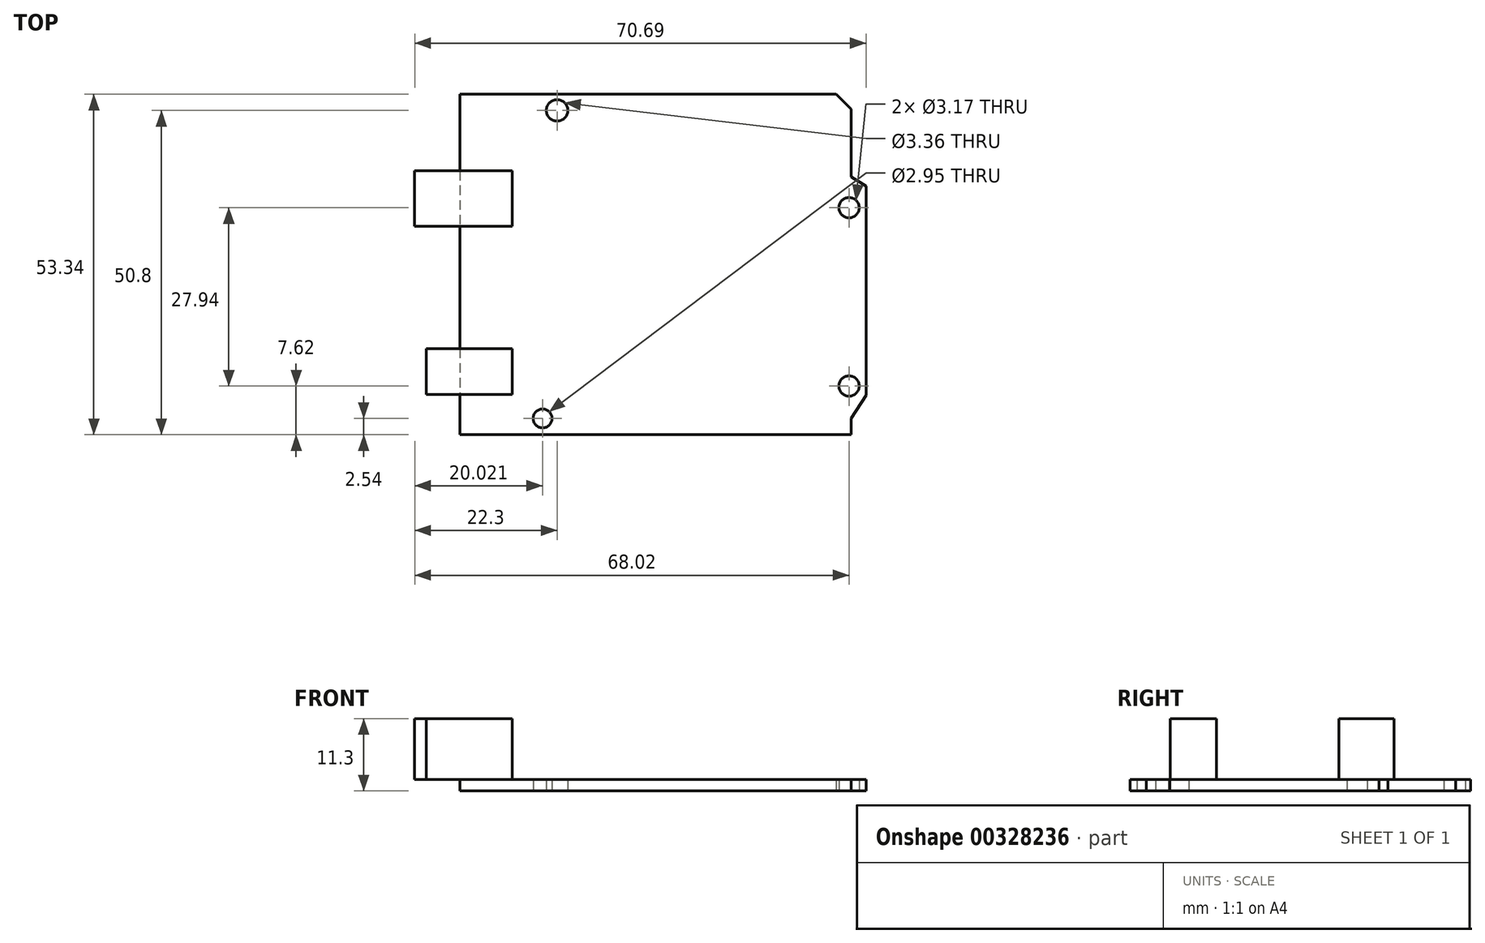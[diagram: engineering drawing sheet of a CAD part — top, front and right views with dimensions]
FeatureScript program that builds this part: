
annotation { "Feature Type Name" : "Feature", "Feature Type Description" : "" }
export const myFeature = defineFeature(function(context is Context, id is Id, definition is map)
    precondition{}
    {
        {
            var Q0;
            Q0=qCreatedBy(makeId("Top.planeOp"),FACE);
            var sketch = newSketch(context, id + "F0", { "sketchPlane" : qUnion([Q0])});
            skLineSegment(sketch, "E0", {"start": v(0, 0) * mm, "end": v(61.27, 0) * mm});
            skLineSegment(sketch, "E1", {"start": v(61.27, 0) * mm, "end": v(61.27, 2.54) * mm});
            skLineSegment(sketch, "E2", {"start": v(0, 53.34) * mm, "end": v(58.91, 53.34) * mm});
            skLineSegment(sketch, "E3", {"start": v(61.27, 50.98) * mm, "end": v(61.27, 40.38) * mm});
            skLineSegment(sketch, "E4", {"start": v(58.91, 53.34) * mm, "end": v(61.27, 50.98) * mm});
            skPoint(sketch, "E5", {"position": v(63.63, 38.97) * mm});
            skLineSegment(sketch, "E6", {"start": v(61.27, 40.38) * mm, "end": v(63.63, 38.97) * mm});
            skCircle(sketch, "E7", {"center": v(12.96, 2.54) * mm, "radius": 1.47 * mm});
            skCircle(sketch, "E8", {"center": v(15.24, 50.8) * mm, "radius": 1.68 * mm});
            skLineSegment(sketch, "E9", {"start": v(63.63, 38.97) * mm, "end": v(63.63, 6.2) * mm});
            skLineSegment(sketch, "E10", {"start": v(63.63, 6.2) * mm, "end": v(61.27, 2.54) * mm});
            skCircle(sketch, "E11", {"center": v(60.96, 35.56) * mm, "radius": 1.59 * mm});
            skCircle(sketch, "E12", {"center": v(60.96, 7.62) * mm, "radius": 1.59 * mm});
            skPoint(sketch, "E13.start.orphan", {"position": v(10.6, 2.95) * mm});
            skLineSegment(sketch, "E14", {"start": v(0, 53.34) * mm, "end": v(0, 0) * mm});
            skSolve(sketch);
        }
        {
            var Q0;
            Q0=qSketchRegion(id+"F0",true);
            extrude(context, id + "F1", {"entities" : qUnion([Q0]), "depth" : 1.78 * mm});
        }
        {
            var Q0;
            Q0=makeQuery(id+"F1.opExtrude","CAP_FACE",FACE,{"disambiguationData":[OSD([sQuery(id+"F0.wireOp",EDGE,"E0"),sQuery(id+"F0.wireOp",EDGE,"E1"),sQuery(id+"F0.wireOp",EDGE,"E2"),sQuery(id+"F0.wireOp",EDGE,"E3"),sQuery(id+"F0.wireOp",EDGE,"E4"),sQuery(id+"F0.wireOp",EDGE,"E6"),sQuery(id+"F0.wireOp",EDGE,"E7"),sQuery(id+"F0.wireOp",EDGE,"E8"),sQuery(id+"F0.wireOp",EDGE,"E9"),sQuery(id+"F0.wireOp",EDGE,"E10"),sQuery(id+"F0.wireOp",EDGE,"E11"),sQuery(id+"F0.wireOp",EDGE,"E12"),sQuery(id+"F0.wireOp",EDGE,"E14")])],"isStart":false});
            var sketch = newSketch(context, id + "F2", { "sketchPlane" : qUnion([Q0])});
            skLineSegment(sketch, "E15.bottom", {"start": v(8.2, 41.34) * mm, "end": v(-7.06, 41.34) * mm});
            skLineSegment(sketch, "E15.top", {"start": v(8.2, 32.67) * mm, "end": v(-7.06, 32.67) * mm});
            skLineSegment(sketch, "E15.left", {"start": v(8.2, 41.34) * mm, "end": v(8.2, 32.67) * mm});
            skLineSegment(sketch, "E15.right", {"start": v(-7.06, 41.34) * mm, "end": v(-7.06, 32.67) * mm});
            skLineSegment(sketch, "E16.bottom", {"start": v(8.2, 13.5) * mm, "end": v(-5.23, 13.5) * mm});
            skLineSegment(sketch, "E16.top", {"start": v(8.2, 6.28) * mm, "end": v(-5.23, 6.28) * mm});
            skLineSegment(sketch, "E16.left", {"start": v(8.2, 13.5) * mm, "end": v(8.2, 6.28) * mm});
            skLineSegment(sketch, "E16.right", {"start": v(-5.23, 13.5) * mm, "end": v(-5.23, 6.28) * mm});
            skSolve(sketch);
        }
        {
            var Q0;
            {var subQ0=sQuery(id+"F2.wireOp",EDGE,"E15.right");Q0=makeQuery(id+"F2.imprint","IMPRINT",FACE,{"disambiguationData":[TD([[makeQuery(id+"F2.imprint","IMPRINT",EDGE,{"derivedFrom":subQ0}),1.0]])]});}
            var Q1;
            {var subQ0=sQuery(id+"F2.wireOp",EDGE,"E16.right");Q1=makeQuery(id+"F2.imprint","IMPRINT",FACE,{"disambiguationData":[TD([[makeQuery(id+"F2.imprint","IMPRINT",EDGE,{"derivedFrom":subQ0}),1.0]])]});}
            var Q2;
            {var subQ0=sQuery(id+"F2.wireOp",EDGE,"E15.left");Q2=makeQuery(id+"F2.imprint","IMPRINT",FACE,{"disambiguationData":[TD([[makeQuery(id+"F2.imprint","IMPRINT",EDGE,{"derivedFrom":subQ0}),-1.0]])]});}
            var Q3;
            {var subQ0=sQuery(id+"F2.wireOp",EDGE,"E16.left");Q3=makeQuery(id+"F2.imprint","IMPRINT",FACE,{"disambiguationData":[TD([[makeQuery(id+"F2.imprint","IMPRINT",EDGE,{"derivedFrom":subQ0}),-1.0]])]});}
            extrude(context, id + "F3", {"entities" : qUnion([Q0, Q1, Q2, Q3]), "depth" : 9.52 * mm});
        }
    });
